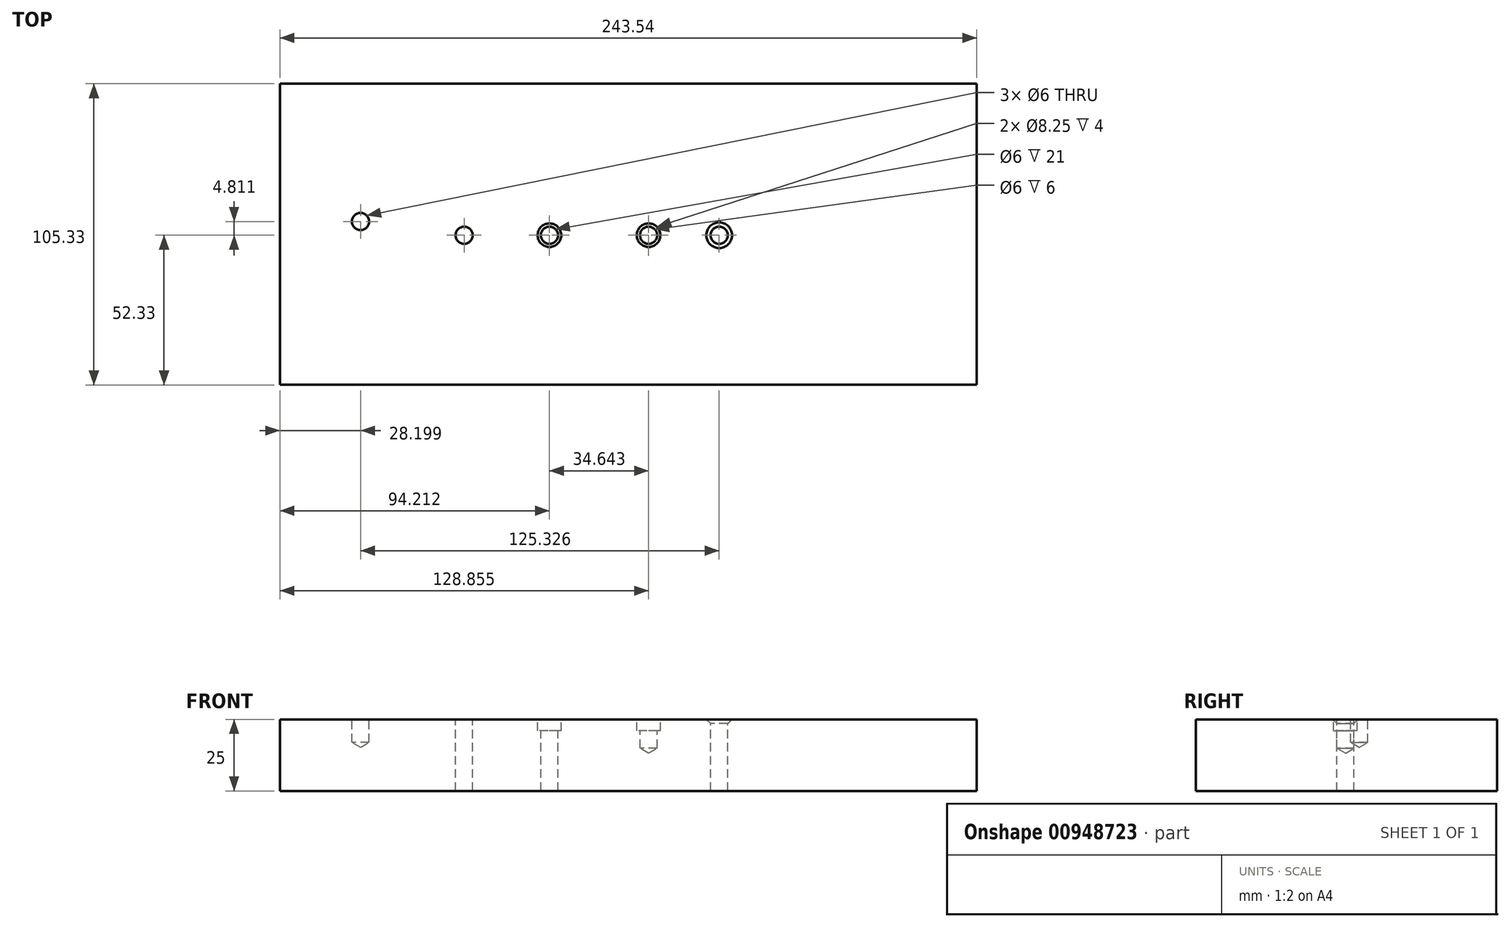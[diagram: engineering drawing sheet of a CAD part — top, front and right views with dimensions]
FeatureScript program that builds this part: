
annotation { "Feature Type Name" : "Feature", "Feature Type Description" : "" }
export const myFeature = defineFeature(function(context is Context, id is Id, definition is map)
    precondition{}
    {
        {
            var Q0;
            Q0=qCreatedBy(makeId("Top.planeOp"),FACE);
            var sketch = newSketch(context, id + "F0", { "sketchPlane" : qUnion([Q0])});
            skLineSegment(sketch, "E0.bottom", {"start": v(-119.87, 53) * mm, "end": v(123.67, 53) * mm});
            skLineSegment(sketch, "E0.top", {"start": v(-119.87, -52.33) * mm, "end": v(123.67, -52.33) * mm});
            skLineSegment(sketch, "E0.left", {"start": v(-119.87, 53) * mm, "end": v(-119.87, -52.33) * mm});
            skLineSegment(sketch, "E0.right", {"start": v(123.67, 53) * mm, "end": v(123.67, -52.33) * mm});
            skSolve(sketch);
        }
        {
            var Q0;
            Q0=makeQuery(id+"F0.imprint","IMPRINT",FACE,{"disambiguationData":[TD([[makeQuery(id+"F0.imprint","IMPRINT",EDGE,{"derivedFrom":sQuery(id+"F0.wireOp",EDGE,"E0.bottom")}),-1.0]])]});
            extrude(context, id + "F1", {"entities" : qUnion([Q0]), "depth" : 25 * mm, "offsetDistance" : 25 * mm});
        }
        {
            var Q0;
            Q0=makeQuery(id+"F1.opExtrude","CAP_FACE",FACE,{"disambiguationData":[OSD([sQuery(id+"F0.wireOp",EDGE,"E0.bottom"),sQuery(id+"F0.wireOp",EDGE,"E0.top"),sQuery(id+"F0.wireOp",EDGE,"E0.left"),sQuery(id+"F0.wireOp",EDGE,"E0.right")])],"isStart":false});
            var sketch = newSketch(context, id + "F2", { "sketchPlane" : qUnion([Q0])});
            skPoint(sketch, "E1", {"position": v(-91.67, 4.81) * mm});
            skPoint(sketch, "E2", {"position": v(-55.47, 0) * mm});
            skPoint(sketch, "E3", {"position": v(-25.66, 0) * mm});
            skPoint(sketch, "E4", {"position": v(8.98, 0) * mm});
            skPoint(sketch, "E5", {"position": v(33.66, 0) * mm});
            skPoint(sketch, "E6", {"position": v(74.89, 0) * mm});
            skSolve(sketch);
        }
        {
            var Q0;
            Q0=sQuery(id+"F2.wireOp",VERTEX,"E1");
            var Q1;
            Q1=makeQuery(id+"F1.opExtrude","SWEPT_BODY",BODY,{"disambiguationData":[OSD([sQuery(id+"F0.wireOp",EDGE,"E0.bottom"),sQuery(id+"F0.wireOp",EDGE,"E0.top"),sQuery(id+"F0.wireOp",EDGE,"E0.left"),sQuery(id+"F0.wireOp",EDGE,"E0.right")])]});
            hole(context, id + "F3", {"style" : HoleStyle.SIMPLE, "endStyle" : HoleEndStyle.BLIND, "holeDiameter" : 6 * mm, "majorDiameter" : 5 * mm, "holeDepth" : 8 * mm, "isTappedThrough" : true, "tappedDepth" : 11.5 * mm, "tapClearance" : 3, "locations" : qUnion([Q0]), "scope" : qUnion([Q1])});
        }
        {
            var Q0;
            Q0=sQuery(id+"F2.wireOp",VERTEX,"E2");
            var Q1;
            Q1=makeQuery(id+"F1.opExtrude","SWEPT_BODY",BODY,{"disambiguationData":[OSD([sQuery(id+"F0.wireOp",EDGE,"E0.bottom"),sQuery(id+"F0.wireOp",EDGE,"E0.top"),sQuery(id+"F0.wireOp",EDGE,"E0.left"),sQuery(id+"F0.wireOp",EDGE,"E0.right")])]});
            hole(context, id + "F4", {"style" : HoleStyle.SIMPLE, "endStyle" : HoleEndStyle.BLIND, "holeDiameter" : 6 * mm, "majorDiameter" : 5 * mm, "holeDepth" : 80 * mm, "isTappedThrough" : true, "tappedDepth" : 11.5 * mm, "tapClearance" : 3, "locations" : qUnion([Q0]), "scope" : qUnion([Q1])});
        }
        {
            var Q0;
            Q0=sQuery(id+"F2.wireOp",VERTEX,"E3");
            var Q1;
            Q1=makeQuery(id+"F1.opExtrude","SWEPT_BODY",BODY,{"disambiguationData":[OSD([sQuery(id+"F0.wireOp",EDGE,"E0.bottom"),sQuery(id+"F0.wireOp",EDGE,"E0.top"),sQuery(id+"F0.wireOp",EDGE,"E0.left"),sQuery(id+"F0.wireOp",EDGE,"E0.right")])]});
            hole(context, id + "F5", {"style" : HoleStyle.C_BORE, "endStyle" : HoleEndStyle.BLIND, "holeDiameter" : 6 * mm, "cBoreDiameter" : 8.25 * mm, "cBoreDepth" : 4 * mm, "majorDiameter" : 5 * mm, "holeDepth" : 80 * mm, "isTappedThrough" : true, "tappedDepth" : 11.5 * mm, "tapClearance" : 3, "locations" : qUnion([Q0]), "scope" : qUnion([Q1])});
        }
        {
            var Q0;
            Q0=sQuery(id+"F2.wireOp",VERTEX,"E4");
            var Q1;
            Q1=makeQuery(id+"F1.opExtrude","SWEPT_BODY",BODY,{"disambiguationData":[OSD([sQuery(id+"F0.wireOp",EDGE,"E0.bottom"),sQuery(id+"F0.wireOp",EDGE,"E0.top"),sQuery(id+"F0.wireOp",EDGE,"E0.left"),sQuery(id+"F0.wireOp",EDGE,"E0.right")])]});
            hole(context, id + "F6", {"style" : HoleStyle.C_BORE, "endStyle" : HoleEndStyle.BLIND, "holeDiameter" : 6 * mm, "cBoreDiameter" : 8.25 * mm, "cBoreDepth" : 4 * mm, "majorDiameter" : 5 * mm, "holeDepth" : 10 * mm, "isTappedThrough" : true, "tappedDepth" : 11.5 * mm, "tapClearance" : 3, "locations" : qUnion([Q0]), "scope" : qUnion([Q1])});
        }
        {
            var Q0;
            Q0=sQuery(id+"F2.wireOp",VERTEX,"E5");
            var Q1;
            Q1=makeQuery(id+"F1.opExtrude","SWEPT_BODY",BODY,{"disambiguationData":[OSD([sQuery(id+"F0.wireOp",EDGE,"E0.bottom"),sQuery(id+"F0.wireOp",EDGE,"E0.top"),sQuery(id+"F0.wireOp",EDGE,"E0.left"),sQuery(id+"F0.wireOp",EDGE,"E0.right")])]});
            hole(context, id + "F7", {"style" : HoleStyle.C_SINK, "endStyle" : HoleEndStyle.BLIND, "holeDiameter" : 6 * mm, "cSinkDiameter" : 8.96 * mm, "cSinkAngle" : 90 * degree, "majorDiameter" : 5 * mm, "holeDepth" : 50 * mm, "isTappedThrough" : true, "tappedDepth" : 11.5 * mm, "tapClearance" : 3, "locations" : qUnion([Q0]), "scope" : qUnion([Q1])});
        }
    });
